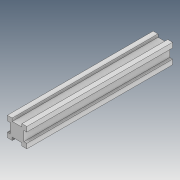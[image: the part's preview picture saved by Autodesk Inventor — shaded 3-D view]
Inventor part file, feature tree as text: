
AUTODESK INVENTOR PART (.ipt)
format: ipt  version: 2021 (Build 250183000, 183)  size: 113,152 bytes
history: native  units: mm
features: other x1, extrude x1, sketch x1
ambient origin geometry x8: Origin, YZ Plane, XZ Plane, XY Plane, X Axis, Y Axis, Z Axis, Center Point
bodies: Body1 (feature_tree)
feature tree (3):
  other  "Sólido1"
  extrude  "Extrusão1"  Depth=5.0mm
  sketch  "Esboço1"  dims[d4=5.0mm d5=5.0mm d6=3.0mm d7=10.0mm d8=3.0mm d9=5.0mm d10=5.0mm d11=3.0mm d12=10.0mm d13=5.0mm d14=5.0mm d15=3.0mm d16=10.0mm d17=3.0mm d18=5.0mm d19=3.0mm d20=10.0mm d21=150.0mm d22=0.0mm]
